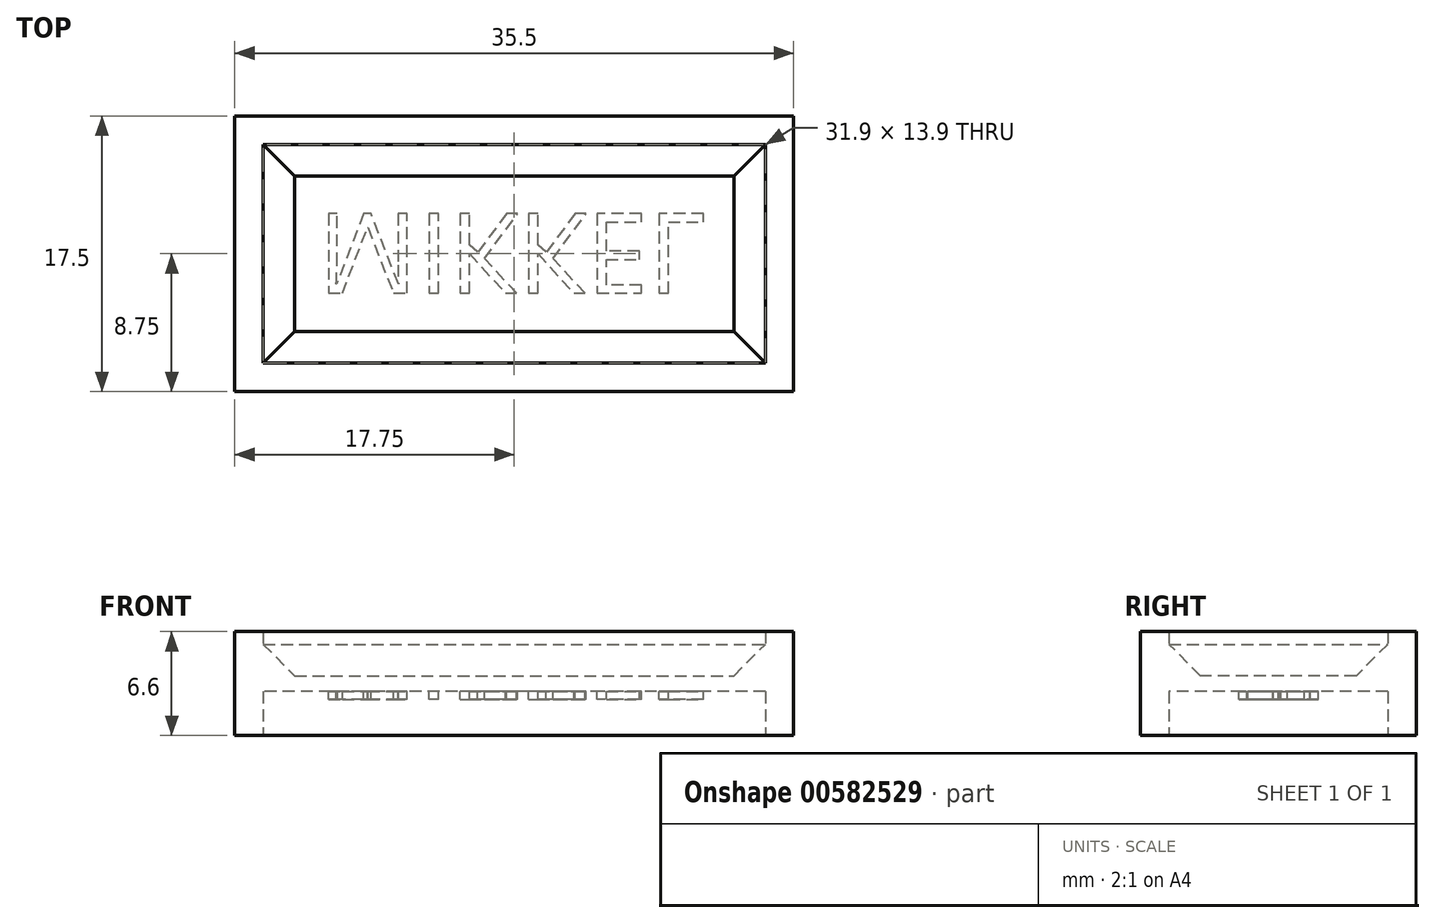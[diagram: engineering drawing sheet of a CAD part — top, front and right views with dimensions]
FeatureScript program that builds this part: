
annotation { "Feature Type Name" : "Feature", "Feature Type Description" : "" }
export const myFeature = defineFeature(function(context is Context, id is Id, definition is map)
    precondition{}
    {
        {
            var Q0;
            Q0=qCreatedBy(makeId("Top.planeOp"),FACE);
            var sketch = newSketch(context, id + "F0", { "sketchPlane" : qUnion([Q0])});
            skLineSegment(sketch, "E0.bottom", {"start": v(17.75, 8.75) * mm, "end": v(-17.75, 8.75) * mm});
            skLineSegment(sketch, "E0.top", {"start": v(17.75, -8.75) * mm, "end": v(-17.75, -8.75) * mm});
            skLineSegment(sketch, "E0.left", {"start": v(17.75, 8.75) * mm, "end": v(17.75, -8.75) * mm});
            skLineSegment(sketch, "E0.right", {"start": v(-17.75, 8.75) * mm, "end": v(-17.75, -8.75) * mm});
            skPoint(sketch, "E0.middle", {"position": v(0, 0) * mm});
            skLineSegment(sketch, "E1.0", {"start": v(-15.95, 6.95) * mm, "end": v(-15.95, -6.95) * mm});
            skLineSegment(sketch, "E1.1", {"start": v(15.95, 6.95) * mm, "end": v(-15.95, 6.95) * mm});
            skLineSegment(sketch, "E1.2", {"start": v(15.95, 6.95) * mm, "end": v(15.95, -6.95) * mm});
            skLineSegment(sketch, "E1.3", {"start": v(15.95, -6.95) * mm, "end": v(-15.95, -6.95) * mm});
            skSolve(sketch);
        }
        {
            var Q0;
            Q0=makeQuery(id+"F0.imprint","IMPRINT",FACE,{"disambiguationData":[TD([[makeQuery(id+"F0.imprint","IMPRINT",EDGE,{"derivedFrom":sQuery(id+"F0.wireOp",EDGE,"E1.0")}),1.0]])]});
            extrude(context, id + "F1", {"entities" : qUnion([Q0]), "endBound" : BoundingType.SYMMETRIC, "depth" : 1 * mm, "offsetDistance" : 25 * mm});
        }
        {
            var Q0;
            Q0=makeQuery(id+"F0.imprint","IMPRINT",FACE,{"disambiguationData":[TD([[makeQuery(id+"F0.imprint","IMPRINT",EDGE,{"derivedFrom":sQuery(id+"F0.wireOp",EDGE,"E0.bottom")}),1.0]])]});
            extrude(context, id + "F2", {"entities" : qUnion([Q0]), "operationType" : NewBodyOperationType.ADD, "endBound" : BoundingType.SYMMETRIC, "depth" : 6.6 * mm, "offsetDistance" : 25 * mm});
        }
        {
            var Q0;
            Q0=makeQuery(id+"F1.opExtrude","CAP_EDGE",EDGE,{"disambiguationData":[OSD([sQuery(id+"F0.wireOp",EDGE,"E1.1")])],"isStart":false});
            var Q1;
            Q1=makeQuery(id+"F1.opExtrude","CAP_EDGE",EDGE,{"disambiguationData":[OSD([sQuery(id+"F0.wireOp",EDGE,"E1.2")])],"isStart":false});
            var Q2;
            Q2=makeQuery(id+"F1.opExtrude","CAP_EDGE",EDGE,{"disambiguationData":[OSD([sQuery(id+"F0.wireOp",EDGE,"E1.3")])],"isStart":false});
            var Q3;
            Q3=makeQuery(id+"F1.opExtrude","CAP_EDGE",EDGE,{"disambiguationData":[OSD([sQuery(id+"F0.wireOp",EDGE,"E1.0")])],"isStart":false});
            var Q4;
            Q4=makeQuery(id+"F1.opExtrude","CAP_EDGE",EDGE,{"disambiguationData":[OSD([sQuery(id+"F0.wireOp",EDGE,"E1.3")])],"isStart":true});
            var Q5;
            Q5=makeQuery(id+"F1.opExtrude","CAP_EDGE",EDGE,{"disambiguationData":[OSD([sQuery(id+"F0.wireOp",EDGE,"E1.0")])],"isStart":true});
            var Q6;
            Q6=makeQuery(id+"F1.opExtrude","CAP_EDGE",EDGE,{"disambiguationData":[OSD([sQuery(id+"F0.wireOp",EDGE,"E1.1")])],"isStart":true});
            var Q7;
            Q7=makeQuery(id+"F1.opExtrude","CAP_EDGE",EDGE,{"disambiguationData":[OSD([sQuery(id+"F0.wireOp",EDGE,"E1.2")])],"isStart":true});
            chamfer(context, id + "F3", {"entities" : qUnion([Q0, Q1, Q2, Q3, Q4, Q5, Q6, Q7]), "width" : 2 * mm, "tangentPropagation" : true});
        }
        {
            var Q0;
            Q0=makeQuery(id+"F1.opExtrude","CAP_FACE",FACE,{"disambiguationData":[OSD([sQuery(id+"F0.wireOp",EDGE,"E1.0"),sQuery(id+"F0.wireOp",EDGE,"E1.1"),sQuery(id+"F0.wireOp",EDGE,"E1.2"),sQuery(id+"F0.wireOp",EDGE,"E1.3")])],"isStart":true});
            var sketch = newSketch(context, id + "F4", { "sketchPlane" : qUnion([Q0])});
            skText(sketch, "E2", { "text": "MIKKEL", "fontName": "OpenSans-Regular.ttf"});
            const initialGuessF4  = {"E2": [-0.0125, -0.00255, 1, 0, 0.0051]};
            skSetInitialGuess(sketch, initialGuessF4);
            skSolve(sketch);
        }
        {
            var Q0;
            Q0 = qSketchRegion(id + "F4", true);
            extrude(context, id + "F5", {"entities" : qUnion([Q0]), "operationType" : NewBodyOperationType.ADD, "depth" : 0.5 * mm, "offsetDistance" : 25 * mm});
        }
    });
